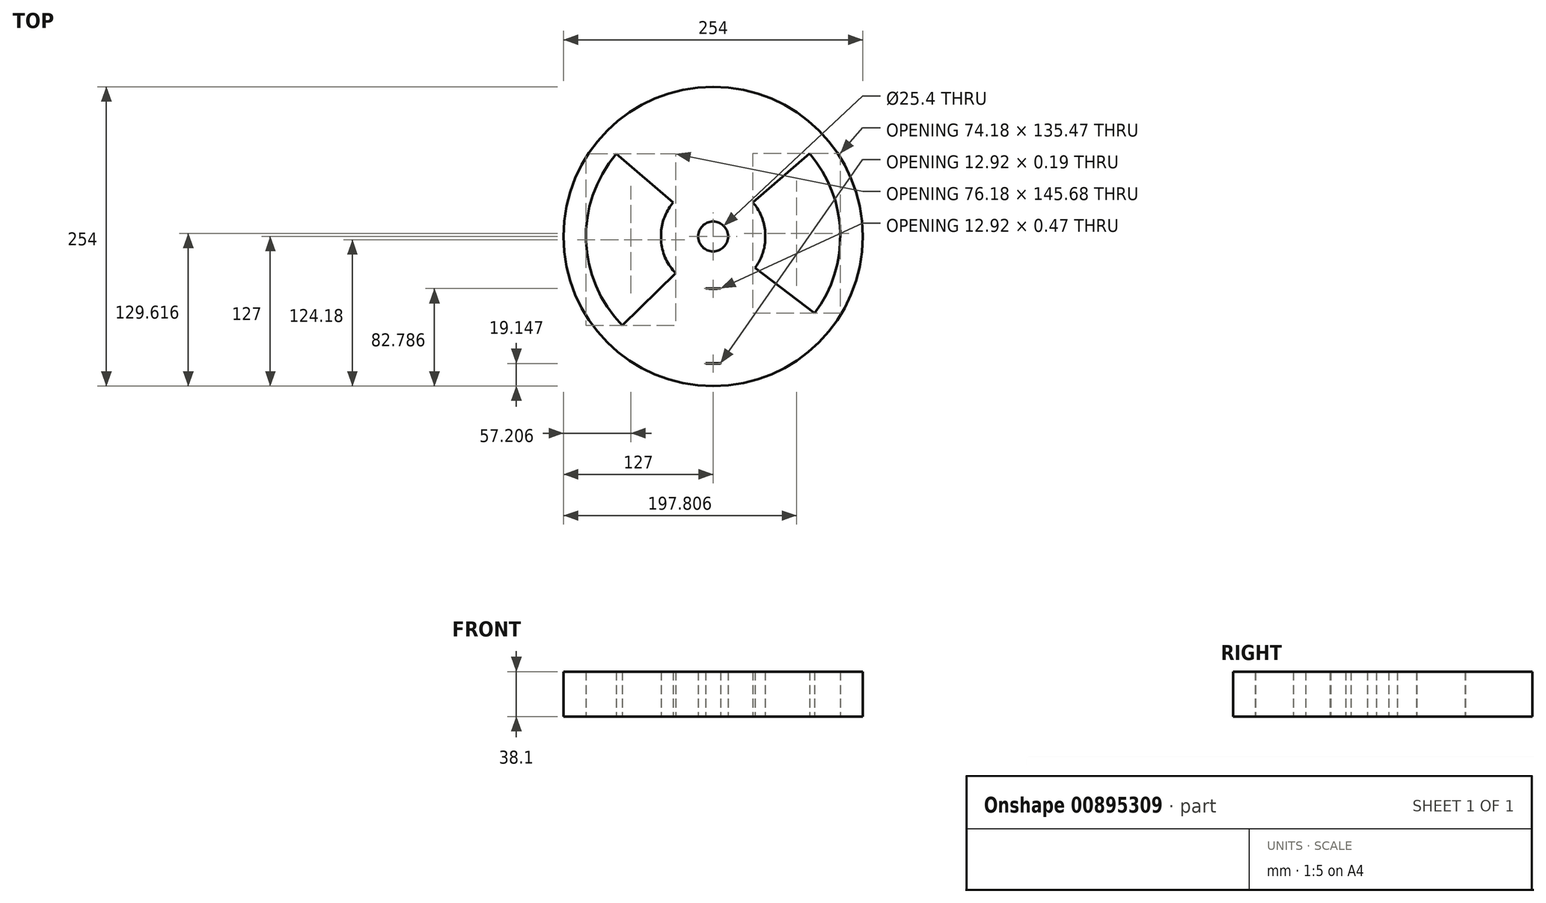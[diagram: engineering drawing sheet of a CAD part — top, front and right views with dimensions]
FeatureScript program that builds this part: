
annotation { "Feature Type Name" : "Feature", "Feature Type Description" : "" }
export const myFeature = defineFeature(function(context is Context, id is Id, definition is map)
    precondition{}
    {
        {
            var Q0;
            Q0=qCreatedBy(makeId("Top.planeOp"),FACE);
            var sketch = newSketch(context, id + "F0", { "sketchPlane" : qUnion([Q0])});
            skCircle(sketch, "E0", {"center": v(0, 0) * mm, "radius": 127 * mm});
            skArc(sketch, "E1", {"start": v(-6.46, 107.76) * mm, "mid": v(0, -107.95) * mm, "end": v(6.46, 107.76) * mm});
            skArc(sketch, "E2", {"start": v(-6.46, 43.98) * mm, "mid": v(0, -44.45) * mm, "end": v(6.46, 43.98) * mm});
            skLineSegment(sketch, "E3", {"start": v(6.46, 107.76) * mm, "end": v(-6.46, 107.76) * mm});
            skLineSegment(sketch, "E4", {"start": v(-6.46, 43.98) * mm, "end": v(6.46, 43.98) * mm});
            skLineSegment(sketch, "E5", {"start": v(107.82, 5.34) * mm, "end": v(107.82, -5.34) * mm});
            skLineSegment(sketch, "E6", {"start": v(44.13, -5.34) * mm, "end": v(44.13, 5.34) * mm});
            skLineSegment(sketch, "E7", {"start": v(-107.82, 5.34) * mm, "end": v(-107.82, -5.34) * mm});
            skLineSegment(sketch, "E8", {"start": v(-44.13, -5.34) * mm, "end": v(-44.13, 5.34) * mm});
            skLineSegment(sketch, "E9", {"start": v(6.46, -107.76) * mm, "end": v(-6.46, -107.76) * mm});
            skLineSegment(sketch, "E10", {"start": v(-6.46, -43.98) * mm, "end": v(6.46, -43.98) * mm});
            skLineSegment(sketch, "E11", {"start": v(33.71, 28.97) * mm, "end": v(81.88, 70.35) * mm});
            skLineSegment(sketch, "E12", {"start": v(-33.83, 28.83) * mm, "end": v(-82.16, 70.02) * mm});
            skLineSegment(sketch, "E13", {"start": v(-31.7, -31.15) * mm, "end": v(-77, -75.66) * mm});
            skLineSegment(sketch, "E14", {"start": v(35.45, -26.81) * mm, "end": v(86.1, -65.12) * mm});
            skCircle(sketch, "E15", {"center": v(0, 0) * mm, "radius": 12.7 * mm});
            skSolve(sketch);
        }
        {
            var Q0;
            Q0=makeQuery(id+"F0.imprint","IMPRINT",FACE,{"disambiguationData":[TD([[makeQuery(id+"F0.imprint","IMPRINT",EDGE,{"derivedFrom":sQuery(id+"F0.wireOp",EDGE,"E0")}),1.0]])]});
            var Q1;
            {var subQ0=sQuery(id+"F0.wireOp",EDGE,"E4");Q1=makeQuery(id+"F0.imprint","IMPRINT",FACE,{"disambiguationData":[TD([[makeQuery(id+"F0.imprint","IMPRINT",EDGE,{"derivedFrom":subQ0}),-1.0]])]});}
            var Q2;
            {var subQ3=sQuery(id+"F0.wireOp",EDGE,"E3");Q2=makeQuery(id+"F0.imprint","IMPRINT",FACE,{"disambiguationData":[TD([[makeQuery(id+"F0.imprint","IMPRINT",EDGE,{"derivedFrom":subQ3}),1.0]])]});}
            var Q3;
            {var subQ4=sQuery(id+"F0.wireOp",EDGE,"E9");Q3=makeQuery(id+"F0.imprint","IMPRINT",FACE,{"disambiguationData":[TD([[makeQuery(id+"F0.imprint","IMPRINT",EDGE,{"derivedFrom":subQ4}),-1.0]])]});}
            extrude(context, id + "F1", {"entities" : qUnion([Q0, Q1, Q2, Q3]), "endBound" : BoundingType.SYMMETRIC, "depth" : 38.1 * mm, "offsetDistance" : 25.4 * mm});
        }
    });
